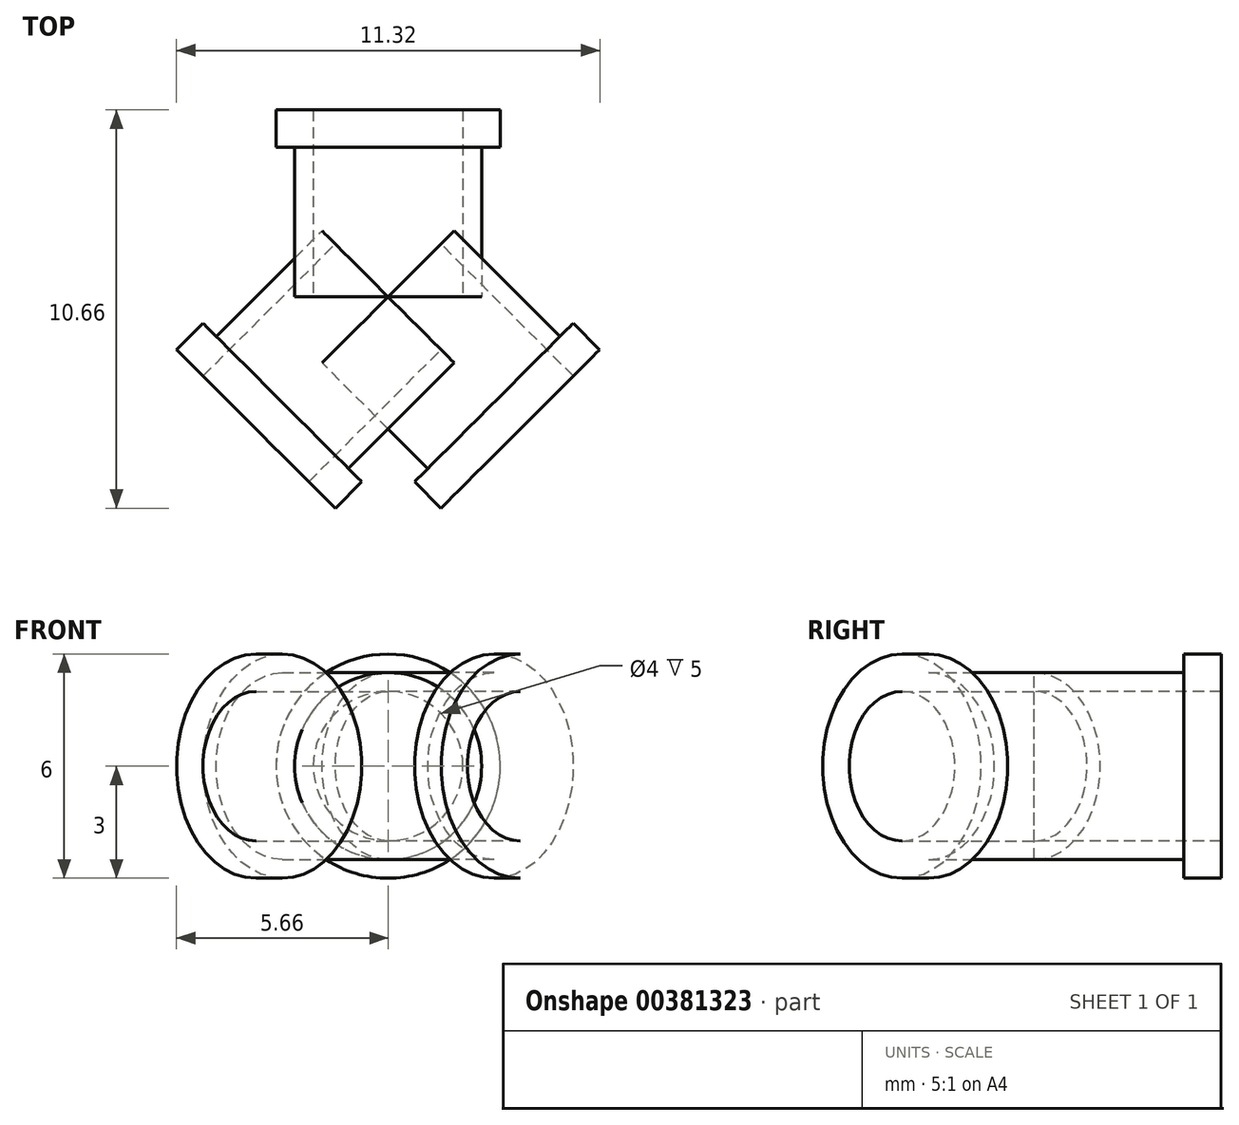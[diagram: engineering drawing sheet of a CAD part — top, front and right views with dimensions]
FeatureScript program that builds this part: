
annotation { "Feature Type Name" : "Feature", "Feature Type Description" : "" }
export const myFeature = defineFeature(function(context is Context, id is Id, definition is map)
    precondition{}
    {
        {
            var Q0;
            Q0=qCreatedBy(makeId("Top.planeOp"),FACE);
            var sketch = newSketch(context, id + "F0", { "sketchPlane" : qUnion([Q0])});
            skLineSegment(sketch, "E0", {"start": v(2, 0) * mm, "end": v(2, 5) * mm});
            skLineSegment(sketch, "E1", {"start": v(2, 5) * mm, "end": v(3, 5) * mm});
            skLineSegment(sketch, "E2", {"start": v(3, 5) * mm, "end": v(3, 4) * mm});
            skLineSegment(sketch, "E3", {"start": v(3, 4) * mm, "end": v(2.5, 4) * mm});
            skLineSegment(sketch, "E4", {"start": v(2.5, 4) * mm, "end": v(2.5, 0) * mm});
            skLineSegment(sketch, "E5", {"start": v(2.5, 0) * mm, "end": v(2, 0) * mm});
            skSolve(sketch);
        }
        {
            var Q0;
            Q0=qCreatedBy(makeId("Top.planeOp"),FACE);
            var sketch = newSketch(context, id + "F1", { "sketchPlane" : qUnion([Q0])});
            skLineSegment(sketch, "E6", {"start": v(0, 0) * mm, "end": v(0, 28.5) * mm, "construction": true});
            skSolve(sketch);
        }
        {
            var Q0;
            Q0=makeQuery(id+"F0.imprint","IMPRINT",FACE,{"disambiguationData":[TD([[makeQuery(id+"F0.imprint","IMPRINT",EDGE,{"derivedFrom":sQuery(id+"F0.wireOp",EDGE,"E0")}),-1.0]])]});
            var Q1;
            Q1=sQuery(id+"F1.wireOp",EDGE,"E6");
            revolve(context, id + "F2", {"entities" : qUnion([Q0]), "axis" : qUnion([Q1]), "revolveType" : RevolveType.FULL});
        }
        {
            var Q0;
            Q0=qCreatedBy(makeId("Front.planeOp"),FACE);
            var sketch = newSketch(context, id + "F3", { "sketchPlane" : qUnion([Q0])});
            skLineSegment(sketch, "E7", {"start": v(0, 0) * mm, "end": v(0, 15.6) * mm, "construction": true});
            skSolve(sketch);
        }
        {
            var Q0;
            Q0=makeQuery(id+"F2.opRevolve","SWEPT_BODY",BODY,{"disambiguationData":[OSD([sQuery(id+"F0.wireOp",EDGE,"E0"),sQuery(id+"F0.wireOp",EDGE,"E1"),sQuery(id+"F0.wireOp",EDGE,"E2"),sQuery(id+"F0.wireOp",EDGE,"E3"),sQuery(id+"F0.wireOp",EDGE,"E4"),sQuery(id+"F0.wireOp",EDGE,"E5")])]});
            var Q1;
            Q1=sQuery(id+"F3.wireOp",EDGE,"E7");
            transform(context, id + "F4", {"entities" : qUnion([Q0]), "transformType" : TransformType.ROTATION, "transformAxis" : qUnion([Q1]), "angle" : 135 * degree, "makeCopy" : true});
        }
        {
            var Q0;
            Q0=makeQuery(id+"F2.opRevolve","SWEPT_BODY",BODY,{"disambiguationData":[OSD([sQuery(id+"F0.wireOp",EDGE,"E0"),sQuery(id+"F0.wireOp",EDGE,"E1"),sQuery(id+"F0.wireOp",EDGE,"E2"),sQuery(id+"F0.wireOp",EDGE,"E3"),sQuery(id+"F0.wireOp",EDGE,"E4"),sQuery(id+"F0.wireOp",EDGE,"E5")])]});
            var Q1;
            Q1=sQuery(id+"F3.wireOp",EDGE,"E7");
            transform(context, id + "F5", {"entities" : qUnion([Q0]), "transformType" : TransformType.ROTATION, "transformAxis" : qUnion([Q1]), "angle" : 225 * degree, "makeCopy" : true});
        }
    });
